# Revit family: puzg-mp3_10m_2_50hz
name_source: partatom
category: 機械設備
units: mm (PartAtom-declared; Revit-internal decimal feet)

## family parameters
OmniClass タイトル = Split System Air Conditioning Units
OmniClass 番号 = 23.75.10.24.21.27.27
パーツ タイプ = 標準
ロード時にボイドで切り取り = いいえ
丸型コネクタ寸法 = 直径を使用
作業面ベース = いいえ
共有 = いいえ
常に垂直 = はい
部屋計算ポイント = いいえ

## types (10) — shared parameters
Clearance Top = 1000
Depth = 330  [stored 1.08268 ft]
IfcExportAs = IfcUnitaryEquipmentType
IfcExportType = AIRCONDITIONINGUNIT
OmniClassCode = 23-33 17 13 11
URL = https://www.mitsubishielectric.co.jp
Uniclass2015Code = Pr_70_65_03_84
Uniclass2015Title = Split coil remote air cooled condensing units
Uniclass2015Version = Systems v1.9
アンカーボルト位置X = 600
アンカーボルト位置Y = 370  [stored 1.21391 ft]
サービススペース = はい
ドレン管径 = 33.00 mm
ユニット2 = はい
ユニット3 = はい
ユニット数 = 1
仕様書バージョン = Version1.0
企業コード = 108420
冷媒管径 = 100.00 mm
分類コード = 50053003126100
参照している仕様書等のバージョン = 公共建築物標準仕様書（機械設備工事編）平成31年度版
周波数 = 50 Hz
呼称 = パッケージ形空気調和機_室外機
始動方式 = インバータ始動方式
形式 = パッケージ形 室外機
本体マテリアル = <カテゴリ別>
極数 = 3
法定耐用年数 = 6
消費電力 = 0 kW
消費電力_冷房 = 0 kW
消費電力_暖房 = 0 kW
発停方法 = 付属スイッチ
相 = 3
積算_科目 = 1 空気調和設備
符号 = PAC
製品出荷対象 = 国内
製造元 = 三菱電機株式会社
設置方法 = 床置形
説明 = 空冷H/P PAC インバータ室外機
負荷分類 = 1_熱源類
運転質量 = 0.00 kg
電動機出力_送風機 = 0 kW
電圧 = 200 V
電源位置Y = 2  [stored 0.00656168 ft]
zero-valued in all types: APF, COP, Clearance Bottom, 価格, 据付ピッチ1

## per-type parameters (varying)
- 室外機_PUZG-MP4MHA2: Clearance Back=100  [stored 0.328084 ft]; Clearance Front=500; Clearance Left=10  [stored 0.0328084 ft]; Clearance Right=10  [stored 0.0328084 ft]; Height=943; Width=950; ドレン　位置X=30  [stored 0.0984252 ft]; ドレン　位置Y=111; ドレン　位置Z=23  [stored 0.0754593 ft]; 冷媒ガス管径=15.88 mm; 冷媒液管径=9.52 mm; 冷媒管位置X=405.5  [stored 1.33038 ft]; 冷媒管位置Y=259.5; 冷媒管位置Z=447; 冷媒管径符号=Bd; 冷媒管（ガス）位置X=434  [stored 1.42388 ft]; 冷媒管（ガス）位置Y=229  [stored 0.751312 ft]; 冷媒管（液）位置X=377  [stored 1.23688 ft]; 冷媒管（液）位置Y=290  [stored 0.951444 ft]; 冷房能力=10 kW; 形名=PUZG-MP4MHA2; 推奨ブレーカー容量=30 A; 暖房能力=11 kW; 最大電流値=21 A; 最小電線太さ_mm2=1.6; 構成品番=PUZG-MP4MHA2; 製品質量=72.00 kg; 質量=86.40 kg; 運転方法=冷暖切替; 電動機出力_圧縮機=3 kW; 電源位置X=275; 電源位置Z=669; 音響パワーレベル（冷）(dB)=69; 音響パワーレベル（暖）(dB)=70
- 室外機_PUZG-MP5MLA2: Clearance Back=150  [stored 0.492126 ft]; Clearance Front=500; Clearance Left=15  [stored 0.0492126 ft]; Clearance Right=15  [stored 0.0492126 ft]; Height=1350; Width=950; ドレン　位置X=50  [stored 0.164042 ft]; ドレン　位置Y=176  [stored 0.577428 ft]; ドレン　位置Z=21  [stored 0.0688976 ft]; 冷媒ガス管径=15.88 mm; 冷媒液管径=9.52 mm; 冷媒管位置X=400.5  [stored 1.31398 ft]; 冷媒管位置Y=260.5  [stored 0.854659 ft]; 冷媒管位置Z=450  [stored 1.47638 ft]; 冷媒管径符号=Bd; 冷媒管（ガス）位置X=429  [stored 1.40748 ft]; 冷媒管（ガス）位置Y=230  [stored 0.754593 ft]; 冷媒管（液）位置X=372  [stored 1.22047 ft]; 冷媒管（液）位置Y=291  [stored 0.954724 ft]; 冷房能力=11 kW; 形名=PUZG-MP5MLA2; 推奨ブレーカー容量=30 A; 暖房能力=14 kW; 最大電流値=24 A; 最小電線太さ_mm2=1.6; 構成品番=PUZG-MP5MLA2; 製品質量=87.00 kg; 質量=104.40 kg; 運転方法=冷暖切替; 電動機出力_圧縮機=3 kW; 電源位置X=325  [stored 1.06627 ft]; 電源位置Z=994; 音響パワーレベル（冷）(dB)=73; 音響パワーレベル（暖）(dB)=74
- 室外機_PUZG-P8MKA2: Clearance Back=150  [stored 0.492126 ft]; Clearance Front=1000; Clearance Left=15  [stored 0.0492126 ft]; Clearance Right=15  [stored 0.0492126 ft]; Height=1338; Width=1050; ドレン　位置X=45  [stored 0.147638 ft]; ドレン　位置Y=176  [stored 0.577428 ft]; ドレン　位置Z=24  [stored 0.0787402 ft]; 冷媒ガス管径=25.40 mm; 冷媒液管径=9.52 mm; 冷媒管位置X=453  [stored 1.48622 ft]; 冷媒管位置Y=282  [stored 0.925197 ft]; 冷媒管位置Z=450  [stored 1.47638 ft]; 冷媒管径符号=Bg; 冷媒管（ガス）位置X=483; 冷媒管（ガス）位置Y=274  [stored 0.89895 ft]; 冷媒管（液）位置X=423  [stored 1.3878 ft]; 冷媒管（液）位置Y=290  [stored 0.951444 ft]; 冷房能力=20 kW; 形名=PUZG-P8_10MKA2 : PUZG-P8KA2; 推奨ブレーカー容量=40 A; 暖房能力=22 kW; 最大電流値=32 A; 最小電線太さ_mm2=2; 構成品番=PUZG-P8MKA2; 製品質量=131.00 kg; 質量=157.20 kg; 運転方法=冷暖切替; 電動機出力_圧縮機=5 kW; 電源位置X=325  [stored 1.06627 ft]; 電源位置Z=1063; 音響パワーレベル（冷）(dB)=79; 音響パワーレベル（暖）(dB)=81
- 室外機_PUZG-MP3MHA2: Clearance Back=100  [stored 0.328084 ft]; Clearance Front=500; Clearance Left=10  [stored 0.0328084 ft]; Clearance Right=10  [stored 0.0328084 ft]; Height=740; Width=950; ドレン　位置X=30  [stored 0.0984252 ft]; ドレン　位置Y=111; ドレン　位置Z=23  [stored 0.0754593 ft]; 冷媒ガス管径=15.88 mm; 冷媒液管径=9.52 mm; 冷媒管位置X=405.5  [stored 1.33038 ft]; 冷媒管位置Y=279.5  [stored 0.916995 ft]; 冷媒管位置Z=295  [stored 0.967848 ft]; 冷媒管径符号=Bd; 冷媒管（ガス）位置X=434  [stored 1.42388 ft]; 冷媒管（ガス）位置Y=269  [stored 0.882546 ft]; 冷媒管（液）位置X=377  [stored 1.23688 ft]; 冷媒管（液）位置Y=290  [stored 0.951444 ft]; 冷房能力=8 kW; 形名=PUZG-MP3MHA2; 推奨ブレーカー容量=20 A; 暖房能力=9 kW; 最大電流値=15 A; 最小電線太さ_mm2=1.6; 構成品番=PUZG-MP3MHA2; 製品質量=59.00 kg; 質量=70.80 kg; 運転方法=冷暖切替; 電動機出力_圧縮機=2 kW; 電源位置X=275; 電源位置Z=459; 音響パワーレベル（冷）(dB)=68; 音響パワーレベル（暖）(dB)=70
- 室外機_PUZG-P10MKA2: Clearance Back=150  [stored 0.492126 ft]; Clearance Front=1000; Clearance Left=15  [stored 0.0492126 ft]; Clearance Right=15  [stored 0.0492126 ft]; Height=1338; Width=1050; ドレン　位置X=45  [stored 0.147638 ft]; ドレン　位置Y=176  [stored 0.577428 ft]; ドレン　位置Z=24  [stored 0.0787402 ft]; 冷媒ガス管径=25.40 mm; 冷媒液管径=12.70 mm; 冷媒管位置X=453  [stored 1.48622 ft]; 冷媒管位置Y=282  [stored 0.925197 ft]; 冷媒管位置Z=424  [stored 1.39108 ft]; 冷媒管径符号=Cg; 冷媒管（ガス）位置X=483; 冷媒管（ガス）位置Y=274  [stored 0.89895 ft]; 冷媒管（液）位置X=423  [stored 1.3878 ft]; 冷媒管（液）位置Y=290  [stored 0.951444 ft]; 冷房能力=24 kW; 形名=PUZG-P8_10MKA2 : PUZG-P10KA2; 推奨ブレーカー容量=50 A; 暖房能力=28 kW; 最大電流値=41 A; 最小電線太さ_mm2=2; 構成品番=PUZG-P10MKA2; 製品質量=140.00 kg; 質量=168.00 kg; 運転方法=冷暖切替; 電動機出力_圧縮機=6 kW; 電源位置X=325  [stored 1.06627 ft]; 電源位置Z=1063; 音響パワーレベル（冷）(dB)=79; 音響パワーレベル（暖）(dB)=81
- 室外機_PUG-MP3MHA2: Clearance Back=100  [stored 0.328084 ft]; Clearance Front=500; Clearance Left=10  [stored 0.0328084 ft]; Clearance Right=10  [stored 0.0328084 ft]; Height=740; Width=950; ドレン　位置X=30  [stored 0.0984252 ft]; ドレン　位置Y=111; ドレン　位置Z=23  [stored 0.0754593 ft]; 冷媒ガス管径=15.88 mm; 冷媒液管径=9.52 mm; 冷媒管位置X=405.5  [stored 1.33038 ft]; 冷媒管位置Y=279.5  [stored 0.916995 ft]; 冷媒管位置Z=295  [stored 0.967848 ft]; 冷媒管径符号=Bd; 冷媒管（ガス）位置X=434  [stored 1.42388 ft]; 冷媒管（ガス）位置Y=269  [stored 0.882546 ft]; 冷媒管（液）位置X=377  [stored 1.23688 ft]; 冷媒管（液）位置Y=290  [stored 0.951444 ft]; 冷房能力=8 kW; 形名=PUZG-MP3MHA2; 推奨ブレーカー容量=20 A; 暖房能力=0 kW; 最大電流値=15 A; 最小電線太さ_mm2=1.6; 構成品番=PUG-MP3MHA2; 製品質量=59.00 kg; 質量=70.80 kg; 運転方法=冷房専用; 電動機出力_圧縮機=2 kW; 電源位置X=275; 電源位置Z=459; 音響パワーレベル（冷）(dB)=68; 音響パワーレベル（暖）(dB)=0
- 室外機_PUG-MP4MHA2: Clearance Back=100  [stored 0.328084 ft]; Clearance Front=500; Clearance Left=10  [stored 0.0328084 ft]; Clearance Right=10  [stored 0.0328084 ft]; Height=943; Width=950; ドレン　位置X=30  [stored 0.0984252 ft]; ドレン　位置Y=111; ドレン　位置Z=23  [stored 0.0754593 ft]; 冷媒ガス管径=15.88 mm; 冷媒液管径=9.52 mm; 冷媒管位置X=405.5  [stored 1.33038 ft]; 冷媒管位置Y=259.5; 冷媒管位置Z=447; 冷媒管径符号=Bd; 冷媒管（ガス）位置X=434  [stored 1.42388 ft]; 冷媒管（ガス）位置Y=229  [stored 0.751312 ft]; 冷媒管（液）位置X=377  [stored 1.23688 ft]; 冷媒管（液）位置Y=290  [stored 0.951444 ft]; 冷房能力=10 kW; 形名=PUZG-MP4MHA2; 推奨ブレーカー容量=30 A; 暖房能力=0 kW; 最大電流値=21 A; 最小電線太さ_mm2=1.6; 構成品番=PUG-MP4MHA2; 製品質量=72.00 kg; 質量=86.40 kg; 運転方法=冷房専用; 電動機出力_圧縮機=3 kW; 電源位置X=275; 電源位置Z=669; 音響パワーレベル（冷）(dB)=69; 音響パワーレベル（暖）(dB)=0
- 室外機_PUG-MP5MLA2: Clearance Back=150  [stored 0.492126 ft]; Clearance Front=500; Clearance Left=15  [stored 0.0492126 ft]; Clearance Right=15  [stored 0.0492126 ft]; Height=1350; Width=950; ドレン　位置X=50  [stored 0.164042 ft]; ドレン　位置Y=176  [stored 0.577428 ft]; ドレン　位置Z=21  [stored 0.0688976 ft]; 冷媒ガス管径=15.88 mm; 冷媒液管径=9.52 mm; 冷媒管位置X=400.5  [stored 1.31398 ft]; 冷媒管位置Y=260.5  [stored 0.854659 ft]; 冷媒管位置Z=450  [stored 1.47638 ft]; 冷媒管径符号=Bd; 冷媒管（ガス）位置X=429  [stored 1.40748 ft]; 冷媒管（ガス）位置Y=230  [stored 0.754593 ft]; 冷媒管（液）位置X=372  [stored 1.22047 ft]; 冷媒管（液）位置Y=291  [stored 0.954724 ft]; 冷房能力=11 kW; 形名=PUZG-MP5MLA2; 推奨ブレーカー容量=30 A; 暖房能力=0 kW; 最大電流値=24 A; 最小電線太さ_mm2=1.6; 構成品番=PUG-MP5MLA2; 製品質量=87.00 kg; 質量=104.40 kg; 運転方法=冷房専用; 電動機出力_圧縮機=3 kW; 電源位置X=325  [stored 1.06627 ft]; 電源位置Z=994; 音響パワーレベル（冷）(dB)=73; 音響パワーレベル（暖）(dB)=0
- 室外機_PUG-P8MKA2: Clearance Back=150  [stored 0.492126 ft]; Clearance Front=1000; Clearance Left=15  [stored 0.0492126 ft]; Clearance Right=15  [stored 0.0492126 ft]; Height=1338; Width=1050; ドレン　位置X=45  [stored 0.147638 ft]; ドレン　位置Y=176  [stored 0.577428 ft]; ドレン　位置Z=24  [stored 0.0787402 ft]; 冷媒ガス管径=25.40 mm; 冷媒液管径=9.52 mm; 冷媒管位置X=453  [stored 1.48622 ft]; 冷媒管位置Y=282  [stored 0.925197 ft]; 冷媒管位置Z=450  [stored 1.47638 ft]; 冷媒管径符号=Bg; 冷媒管（ガス）位置X=483; 冷媒管（ガス）位置Y=274  [stored 0.89895 ft]; 冷媒管（液）位置X=423  [stored 1.3878 ft]; 冷媒管（液）位置Y=290  [stored 0.951444 ft]; 冷房能力=20 kW; 形名=PUZG-P8_10MKA2 : PUZG-P8KA2; 推奨ブレーカー容量=40 A; 暖房能力=0 kW; 最大電流値=32 A; 最小電線太さ_mm2=2; 構成品番=PUG-P8MKA2; 製品質量=131.00 kg; 質量=157.20 kg; 運転方法=冷房専用; 電動機出力_圧縮機=5 kW; 電源位置X=325  [stored 1.06627 ft]; 電源位置Z=1063; 音響パワーレベル（冷）(dB)=79; 音響パワーレベル（暖）(dB)=0
- 室外機_PUG-P10MKA2: Clearance Back=150  [stored 0.492126 ft]; Clearance Front=1000; Clearance Left=15  [stored 0.0492126 ft]; Clearance Right=15  [stored 0.0492126 ft]; Height=1338; Width=1050; ドレン　位置X=45  [stored 0.147638 ft]; ドレン　位置Y=176  [stored 0.577428 ft]; ドレン　位置Z=24  [stored 0.0787402 ft]; 冷媒ガス管径=25.40 mm; 冷媒液管径=12.70 mm; 冷媒管位置X=453  [stored 1.48622 ft]; 冷媒管位置Y=282  [stored 0.925197 ft]; 冷媒管位置Z=424  [stored 1.39108 ft]; 冷媒管径符号=Cg; 冷媒管（ガス）位置X=483; 冷媒管（ガス）位置Y=274  [stored 0.89895 ft]; 冷媒管（液）位置X=423  [stored 1.3878 ft]; 冷媒管（液）位置Y=290  [stored 0.951444 ft]; 冷房能力=24 kW; 形名=PUZG-P8_10MKA2 : PUZG-P10KA2; 推奨ブレーカー容量=50 A; 暖房能力=0 kW; 最大電流値=41 A; 最小電線太さ_mm2=2; 構成品番=PUG-P10MKA2; 製品質量=140.00 kg; 質量=168.00 kg; 運転方法=冷房専用; 電動機出力_圧縮機=6 kW; 電源位置X=325  [stored 1.06627 ft]; 電源位置Z=1063; 音響パワーレベル（冷）(dB)=79; 音響パワーレベル（暖）(dB)=0

note: [stored X ft] marks values corroborated as IEEE doubles in the binary element streams (Revit-internal decimal feet)
